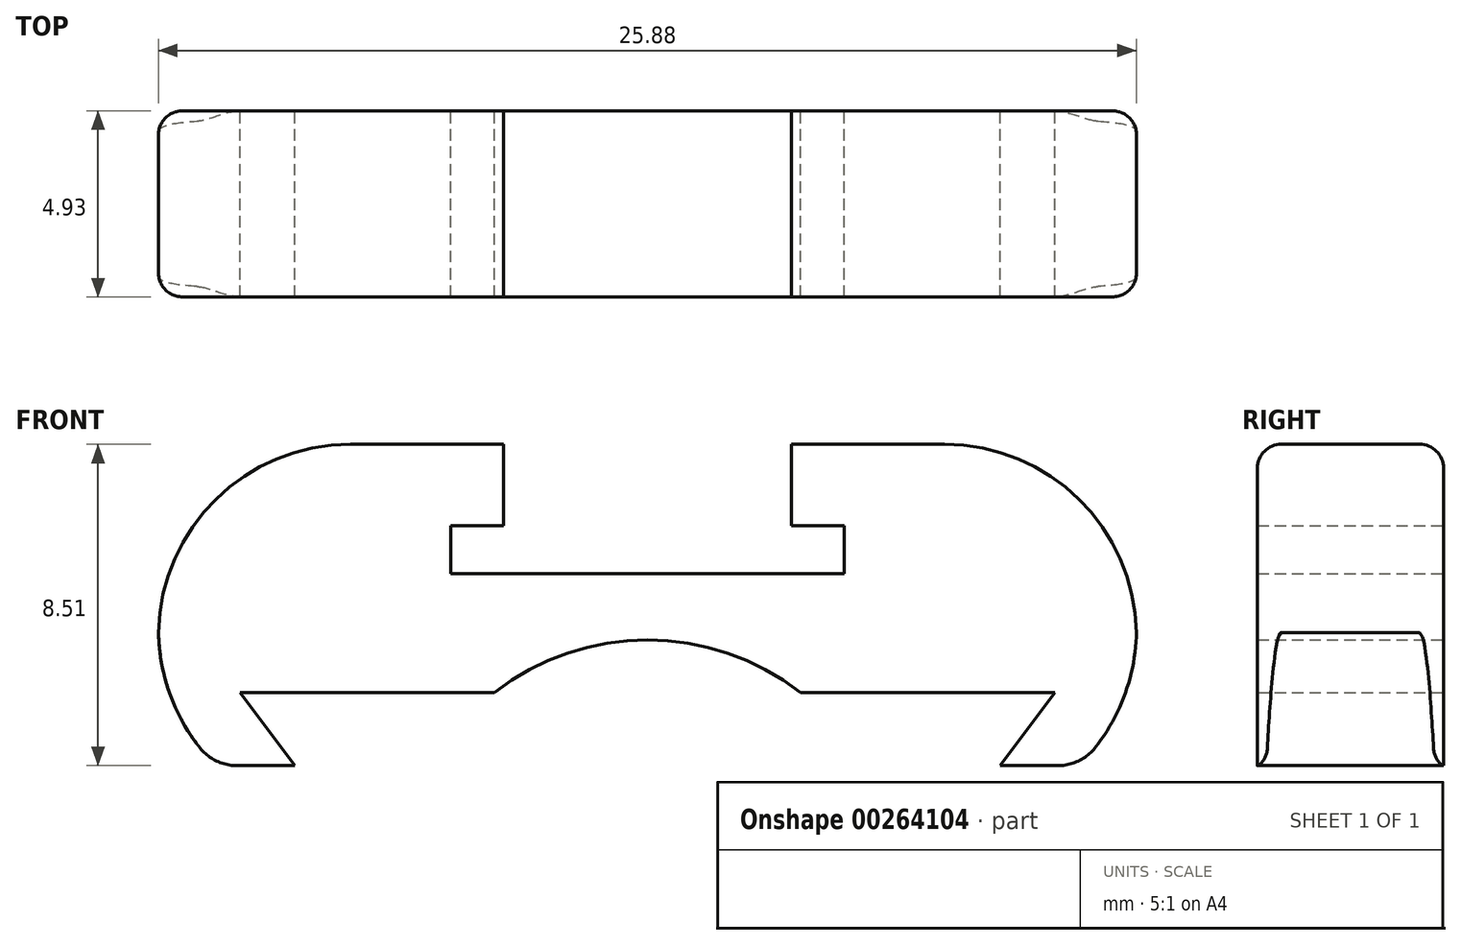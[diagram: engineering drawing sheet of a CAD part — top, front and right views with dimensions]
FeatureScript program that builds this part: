
annotation { "Feature Type Name" : "Feature", "Feature Type Description" : "" }
export const myFeature = defineFeature(function(context is Context, id is Id, definition is map)
    precondition{}
    {
        {
            var Q0;
            Q0=qCreatedBy(makeId("Front.planeOp"),FACE);
            var sketch = newSketch(context, id + "F0", { "sketchPlane" : qUnion([Q0])});
            skLineSegment(sketch, "E0", {"start": v(0, 3.15) * mm, "end": v(5.2, 3.15) * mm});
            skLineSegment(sketch, "E1", {"start": v(12.94, 0) * mm, "end": v(11.5, -1.93) * mm});
            skLineSegment(sketch, "E2", {"start": v(11.5, -1.93) * mm, "end": v(9.33, -1.93) * mm});
            skLineSegment(sketch, "E3", {"start": v(9.33, -1.93) * mm, "end": v(10.78, 0) * mm});
            skLineSegment(sketch, "E4", {"start": v(4.05, 0) * mm, "end": v(10.78, 0) * mm});
            skLineSegment(sketch, "E5", {"start": v(12.94, 0) * mm, "end": v(12.94, 6.58) * mm});
            skLineSegment(sketch, "E6", {"start": v(12.94, 6.58) * mm, "end": v(3.8, 6.58) * mm});
            skLineSegment(sketch, "E7", {"start": v(3.8, 6.58) * mm, "end": v(3.81, 4.42) * mm});
            skLineSegment(sketch, "E8", {"start": v(3.81, 4.42) * mm, "end": v(5.2, 4.42) * mm});
            skLineSegment(sketch, "E9", {"start": v(5.2, 4.42) * mm, "end": v(5.2, 3.15) * mm});
            skLineSegment(sketch, "E10", {"start": v(0, 0) * mm, "end": v(0, 11.26) * mm, "construction": true});
            skLineSegment(sketch, "E11.MirrorCS", {"start": v(-11.5, -1.93) * mm, "end": v(-9.33, -1.93) * mm});
            skLineSegment(sketch, "E12.MirrorCS", {"start": v(0, 3.15) * mm, "end": v(-5.2, 3.15) * mm});
            skLineSegment(sketch, "E13.MirrorCS", {"start": v(-9.33, -1.93) * mm, "end": v(-10.78, 0) * mm});
            skLineSegment(sketch, "E14.MirrorCS", {"start": v(-3.81, 4.42) * mm, "end": v(-5.2, 4.42) * mm});
            skLineSegment(sketch, "E15.MirrorCS", {"start": v(-4.05, 0) * mm, "end": v(-10.78, 0) * mm});
            skLineSegment(sketch, "E16.MirrorCS", {"start": v(-5.2, 4.42) * mm, "end": v(-5.2, 3.15) * mm});
            skLineSegment(sketch, "E17.MirrorCS", {"start": v(-12.94, 0) * mm, "end": v(-11.5, -1.93) * mm});
            skLineSegment(sketch, "E18.MirrorCS", {"start": v(-12.94, 0) * mm, "end": v(-12.94, 6.58) * mm});
            skLineSegment(sketch, "E19.MirrorCS", {"start": v(-12.94, 6.58) * mm, "end": v(-3.8, 6.58) * mm});
            skLineSegment(sketch, "E20.MirrorCS", {"start": v(-3.8, 6.58) * mm, "end": v(-3.81, 4.42) * mm});
            skArc(sketch, "E21", {"start": v(4.05, 0) * mm, "mid": v(0, 1.4) * mm, "end": v(-4.05, 0) * mm});
            skPoint(sketch, "E22.orphan", {"position": v(0, 0) * mm});
            skSolve(sketch);
        }
        {
            var Q0;
            Q0=makeQuery(id+"F0.imprint","IMPRINT",FACE,{"disambiguationData":[TD([[makeQuery(id+"F0.imprint","IMPRINT",EDGE,{"derivedFrom":sQuery(id+"F0.wireOp",EDGE,"E0")}),-1.0]])]});
            extrude(context, id + "F1", {"entities" : qUnion([Q0]), "depth" : 4.93 * mm});
        }
        {
            var Q0;
            Q0=makeQuery(id+"F1.opExtrude","SWEPT_EDGE",EDGE,{"disambiguationData":[OSD([sQuery(id+"F0.wireOp",EDGE,"E17.MirrorCS"),sQuery(id+"F0.wireOp",EDGE,"E18.MirrorCS")])]});
            var Q1;
            Q1=makeQuery(id+"F1.opExtrude","SWEPT_EDGE",EDGE,{"disambiguationData":[OSD([sQuery(id+"F0.wireOp",EDGE,"E1"),sQuery(id+"F0.wireOp",EDGE,"E5")])]});
            var Q2;
            Q2=makeQuery(id+"F1.opExtrude","SWEPT_EDGE",EDGE,{"disambiguationData":[OSD([sQuery(id+"F0.wireOp",EDGE,"E5"),sQuery(id+"F0.wireOp",EDGE,"E6")])]});
            var Q3;
            Q3=makeQuery(id+"F1.opExtrude","SWEPT_EDGE",EDGE,{"disambiguationData":[OSD([sQuery(id+"F0.wireOp",EDGE,"E18.MirrorCS"),sQuery(id+"F0.wireOp",EDGE,"E19.MirrorCS")])]});
            fillet(context, id + "F2", {"entities" : qUnion([Q0, Q1, Q2, Q3]), "radius" : 5.08 * mm, "tangentPropagation" : true, "allowEdgeOverflow" : false});
        }
        {
            var Q0;
            Q0=makeQuery(id+"F1.opExtrude","CAP_EDGE",EDGE,{"disambiguationData":[OSD([sQuery(id+"F0.wireOp",EDGE,"E19.MirrorCS")])],"isStart":false});
            var Q1;
            Q1=makeQuery(id+"F1.opExtrude","CAP_EDGE",EDGE,{"disambiguationData":[OSD([sQuery(id+"F0.wireOp",EDGE,"E6")])],"isStart":false});
            var Q2;
            {var subQ0=sQuery(id+"F0.wireOp",EDGE,"E6");var subQ1=sQuery(id+"F0.wireOp",EDGE,"E5");Q2=makeQuery(id+"F2.opFillet","BLEND_EDGE",EDGE,{"blendedFrom":[makeQuery(id+"F1.opExtrude","SWEPT_EDGE",EDGE,{"disambiguationData":[OSD([subQ1,subQ0])]}),makeQuery(id+"F1.opExtrude","CAP_FACE",FACE,{"disambiguationData":[OSD([sQuery(id+"F0.wireOp",EDGE,"E0"),sQuery(id+"F0.wireOp",EDGE,"E1"),sQuery(id+"F0.wireOp",EDGE,"E2"),sQuery(id+"F0.wireOp",EDGE,"E3"),sQuery(id+"F0.wireOp",EDGE,"E4"),subQ1,subQ0,sQuery(id+"F0.wireOp",EDGE,"E7"),sQuery(id+"F0.wireOp",EDGE,"E8"),sQuery(id+"F0.wireOp",EDGE,"E9"),sQuery(id+"F0.wireOp",EDGE,"E11.MirrorCS"),sQuery(id+"F0.wireOp",EDGE,"E12.MirrorCS"),sQuery(id+"F0.wireOp",EDGE,"E13.MirrorCS"),sQuery(id+"F0.wireOp",EDGE,"E14.MirrorCS"),sQuery(id+"F0.wireOp",EDGE,"E15.MirrorCS"),sQuery(id+"F0.wireOp",EDGE,"E16.MirrorCS"),sQuery(id+"F0.wireOp",EDGE,"E17.MirrorCS"),sQuery(id+"F0.wireOp",EDGE,"E18.MirrorCS"),sQuery(id+"F0.wireOp",EDGE,"E19.MirrorCS"),sQuery(id+"F0.wireOp",EDGE,"E20.MirrorCS"),sQuery(id+"F0.wireOp",EDGE,"E21")])],"isStart":true})],"blendedInto":[makeQuery(id+"F1.opExtrude","CAP_FACE",FACE,{"disambiguationData":[OSD([sQuery(id+"F0.wireOp",EDGE,"E0"),sQuery(id+"F0.wireOp",EDGE,"E1"),sQuery(id+"F0.wireOp",EDGE,"E2"),sQuery(id+"F0.wireOp",EDGE,"E3"),sQuery(id+"F0.wireOp",EDGE,"E4"),subQ1,subQ0,sQuery(id+"F0.wireOp",EDGE,"E7"),sQuery(id+"F0.wireOp",EDGE,"E8"),sQuery(id+"F0.wireOp",EDGE,"E9"),sQuery(id+"F0.wireOp",EDGE,"E11.MirrorCS"),sQuery(id+"F0.wireOp",EDGE,"E12.MirrorCS"),sQuery(id+"F0.wireOp",EDGE,"E13.MirrorCS"),sQuery(id+"F0.wireOp",EDGE,"E14.MirrorCS"),sQuery(id+"F0.wireOp",EDGE,"E15.MirrorCS"),sQuery(id+"F0.wireOp",EDGE,"E16.MirrorCS"),sQuery(id+"F0.wireOp",EDGE,"E17.MirrorCS"),sQuery(id+"F0.wireOp",EDGE,"E18.MirrorCS"),sQuery(id+"F0.wireOp",EDGE,"E19.MirrorCS"),sQuery(id+"F0.wireOp",EDGE,"E20.MirrorCS"),sQuery(id+"F0.wireOp",EDGE,"E21")])],"isStart":true})]});}
            var Q3;
            {var subQ0=sQuery(id+"F0.wireOp",EDGE,"E19.MirrorCS");var subQ1=sQuery(id+"F0.wireOp",EDGE,"E18.MirrorCS");Q3=makeQuery(id+"F2.opFillet","BLEND_EDGE",EDGE,{"blendedFrom":[makeQuery(id+"F1.opExtrude","SWEPT_EDGE",EDGE,{"disambiguationData":[OSD([subQ1,subQ0])]}),makeQuery(id+"F1.opExtrude","CAP_FACE",FACE,{"disambiguationData":[OSD([sQuery(id+"F0.wireOp",EDGE,"E0"),sQuery(id+"F0.wireOp",EDGE,"E1"),sQuery(id+"F0.wireOp",EDGE,"E2"),sQuery(id+"F0.wireOp",EDGE,"E3"),sQuery(id+"F0.wireOp",EDGE,"E4"),sQuery(id+"F0.wireOp",EDGE,"E5"),sQuery(id+"F0.wireOp",EDGE,"E6"),sQuery(id+"F0.wireOp",EDGE,"E7"),sQuery(id+"F0.wireOp",EDGE,"E8"),sQuery(id+"F0.wireOp",EDGE,"E9"),sQuery(id+"F0.wireOp",EDGE,"E11.MirrorCS"),sQuery(id+"F0.wireOp",EDGE,"E12.MirrorCS"),sQuery(id+"F0.wireOp",EDGE,"E13.MirrorCS"),sQuery(id+"F0.wireOp",EDGE,"E14.MirrorCS"),sQuery(id+"F0.wireOp",EDGE,"E15.MirrorCS"),sQuery(id+"F0.wireOp",EDGE,"E16.MirrorCS"),sQuery(id+"F0.wireOp",EDGE,"E17.MirrorCS"),subQ1,subQ0,sQuery(id+"F0.wireOp",EDGE,"E20.MirrorCS"),sQuery(id+"F0.wireOp",EDGE,"E21")])],"isStart":true})],"blendedInto":[makeQuery(id+"F1.opExtrude","CAP_FACE",FACE,{"disambiguationData":[OSD([sQuery(id+"F0.wireOp",EDGE,"E0"),sQuery(id+"F0.wireOp",EDGE,"E1"),sQuery(id+"F0.wireOp",EDGE,"E2"),sQuery(id+"F0.wireOp",EDGE,"E3"),sQuery(id+"F0.wireOp",EDGE,"E4"),sQuery(id+"F0.wireOp",EDGE,"E5"),sQuery(id+"F0.wireOp",EDGE,"E6"),sQuery(id+"F0.wireOp",EDGE,"E7"),sQuery(id+"F0.wireOp",EDGE,"E8"),sQuery(id+"F0.wireOp",EDGE,"E9"),sQuery(id+"F0.wireOp",EDGE,"E11.MirrorCS"),sQuery(id+"F0.wireOp",EDGE,"E12.MirrorCS"),sQuery(id+"F0.wireOp",EDGE,"E13.MirrorCS"),sQuery(id+"F0.wireOp",EDGE,"E14.MirrorCS"),sQuery(id+"F0.wireOp",EDGE,"E15.MirrorCS"),sQuery(id+"F0.wireOp",EDGE,"E16.MirrorCS"),sQuery(id+"F0.wireOp",EDGE,"E17.MirrorCS"),subQ1,subQ0,sQuery(id+"F0.wireOp",EDGE,"E20.MirrorCS"),sQuery(id+"F0.wireOp",EDGE,"E21")])],"isStart":true})]});}
            fillet(context, id + "F3", {"entities" : qUnion([Q0, Q1, Q2, Q3]), "radius" : 0.64 * mm, "tangentPropagation" : true, "allowEdgeOverflow" : false});
        }
        {
            var Q0;
            Q0=makeQuery(id+"F1.opExtrude","SWEPT_EDGE",EDGE,{"disambiguationData":[OSD([sQuery(id+"F0.wireOp",EDGE,"E11.MirrorCS"),sQuery(id+"F0.wireOp",EDGE,"E17.MirrorCS")])]});
            var Q1;
            Q1=makeQuery(id+"F1.opExtrude","SWEPT_EDGE",EDGE,{"disambiguationData":[OSD([sQuery(id+"F0.wireOp",EDGE,"E1"),sQuery(id+"F0.wireOp",EDGE,"E2")])]});
            fillet(context, id + "F4", {"entities" : qUnion([Q0, Q1]), "radius" : 1.27 * mm, "tangentPropagation" : true, "allowEdgeOverflow" : false});
        }
    });
